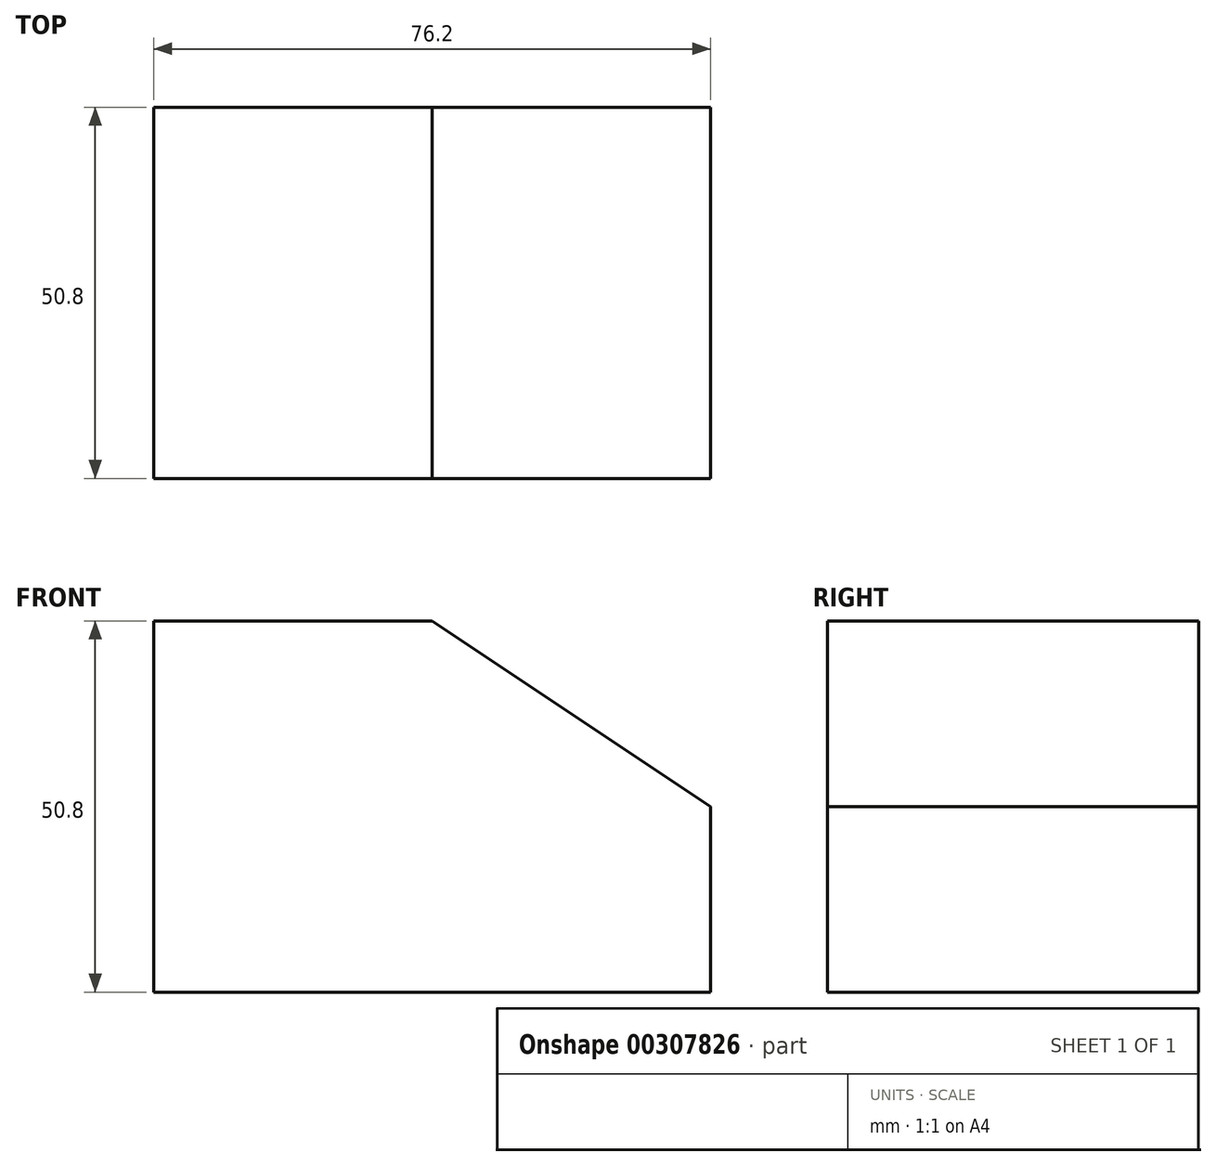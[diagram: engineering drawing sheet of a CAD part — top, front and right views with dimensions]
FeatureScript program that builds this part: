
annotation { "Feature Type Name" : "Feature", "Feature Type Description" : "" }
export const myFeature = defineFeature(function(context is Context, id is Id, definition is map)
    precondition{}
    {
        {
            var Q0;
            Q0=qCreatedBy(makeId("Front.planeOp"),FACE);
            var sketch = newSketch(context, id + "F0", { "sketchPlane" : qUnion([Q0])});
            skLineSegment(sketch, "E0", {"start": v(-33.15, 25.4) * mm, "end": v(-33.15, -25.4) * mm});
            skLineSegment(sketch, "E1", {"start": v(-33.15, -25.4) * mm, "end": v(43.05, -25.4) * mm});
            skLineSegment(sketch, "E2", {"start": v(43.05, -25.4) * mm, "end": v(43.05, 0) * mm});
            skLineSegment(sketch, "E3", {"start": v(43.05, 0) * mm, "end": v(4.95, 25.4) * mm});
            skLineSegment(sketch, "E4", {"start": v(-33.15, 25.4) * mm, "end": v(4.95, 25.4) * mm});
            skSolve(sketch);
        }
        {
            var Q0;
            Q0=makeQuery(id+"F0.imprint","IMPRINT",FACE,{"disambiguationData":[TD([[makeQuery(id+"F0.imprint","IMPRINT",EDGE,{"derivedFrom":sQuery(id+"F0.wireOp",EDGE,"E0")}),1.0]])]});
            extrude(context, id + "F1", {"entities" : qUnion([Q0]), "depth" : 50.8 * mm});
        }
    });
